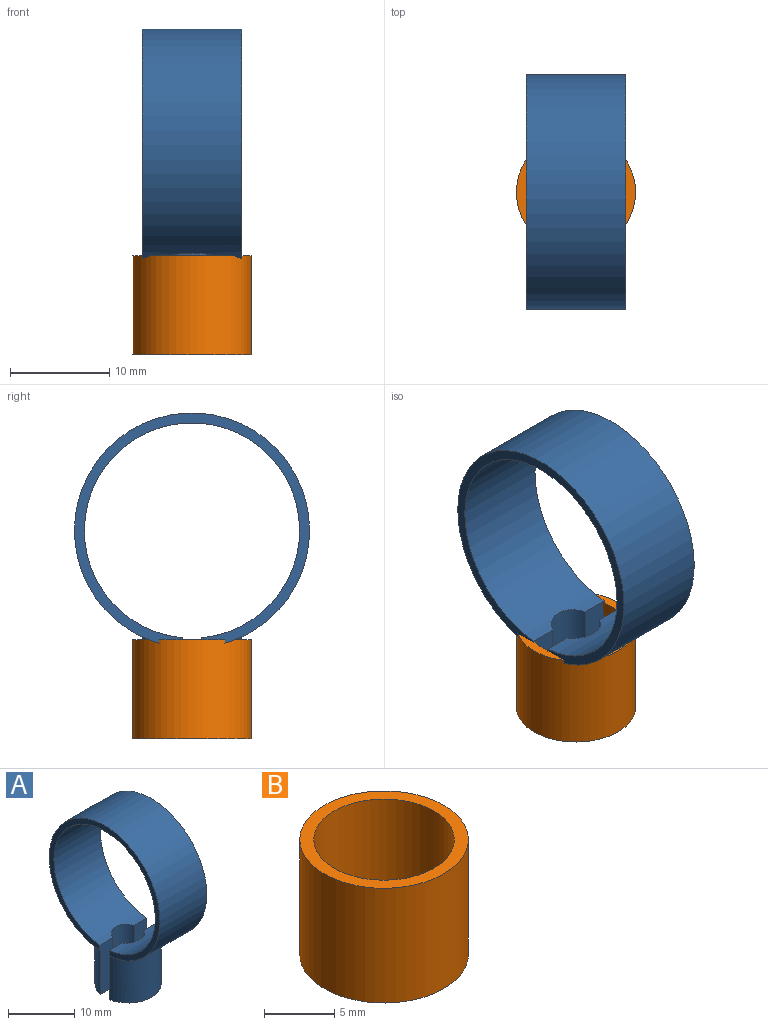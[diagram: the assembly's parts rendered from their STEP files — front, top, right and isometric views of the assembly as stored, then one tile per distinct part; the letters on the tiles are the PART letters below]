
ASSEMBLY  parts=2 mates=1
PART A: 14 faces, bbox 10x23.7x31.9 mm
  f0: cylinder r=10.85mm len=21.7mm, axis (-1,0,0), area 651.7mm2, adj f6,f7,f8,f9,f10,f11,f12,f13
  f1: cylinder r=5mm len=9.8mm, axis (0,0,1), area 120.2mm2, adj f3,f5,f12,f13
  f2: cylinder r=5mm len=9.8mm, axis (0,0,1), area 120.2mm2, adj f4,f5,f10,f11
  f3: plane 9.8x4mm, normal (0,0,-1), area 24.4mm2, adj f1,f8,f12,f13
  f4: plane 9.8x4mm, normal (0,0,-1), area 24.4mm2, adj f2,f9,f10,f11
  f5: cylinder r=11.85mm len=23.7mm, axis (-1,0,0), area 664mm2, adj f1,f2,f6,f7,f10,f11,f12,f13
  f6: plane 23.7x23.66mm, normal (1,0,0), area 69.3mm2, adj f0,f5,f11,f12
  f7: plane 23.7x23.66mm, normal (-1,0,0), area 69.3mm2, adj f0,f5,f10,f13
  f8: cylinder r=2.5mm len=9.44mm, axis (0,0,-1), area 54.1mm2, adj f0,f3,f12,f13
  f9: cylinder r=2.5mm len=9.44mm, axis (0,0,-1), area 54.1mm2, adj f0,f4,f10,f11
  f10: plane 9.2x2.71mm, normal (0,1,0), area 24.1mm2, adj f0,f2,f4,f5,f7,f9
  f11: plane 9.2x2.71mm, normal (0,1,0), area 24.1mm2, adj f0,f2,f4,f5,f6,f9
  f12: plane 9.2x2.71mm, normal (0,-1,0), area 24.1mm2, adj f0,f1,f3,f5,f6,f8
  f13: plane 9.2x2.71mm, normal (0,-1,0), area 24.1mm2, adj f0,f1,f3,f5,f7,f8
PART B: 6 faces, bbox 12x12x10 mm
  f0: plane 12x12mm, normal (0,0,1), area 34.6mm2, adj f1,f5
  f1: cylinder r=6mm len=12mm, axis (0,0,1), area 377mm2, adj f0,f2
  f2: plane 12x12mm, normal (0,0,-1), area 84.8mm2, adj f1,f3
  f3: cylinder r=3mm len=6mm, axis (0,0,1), area 18.8mm2, adj f2,f4
  f4: plane 10x10mm, normal (0,0,1), area 50.3mm2, adj f3,f5
  f5: cylinder r=5mm len=10mm, axis (0,0,1), area 282.7mm2, adj f0,f4
PLACE A t=(-17.48,1.37,1.76)mm
PLACE B t=(-17.48,1.37,1.76)mm
MATE fastened B.f1 <-> A.f1  axis (0,0,1) through (-17.48,1.37,1.76)mm
